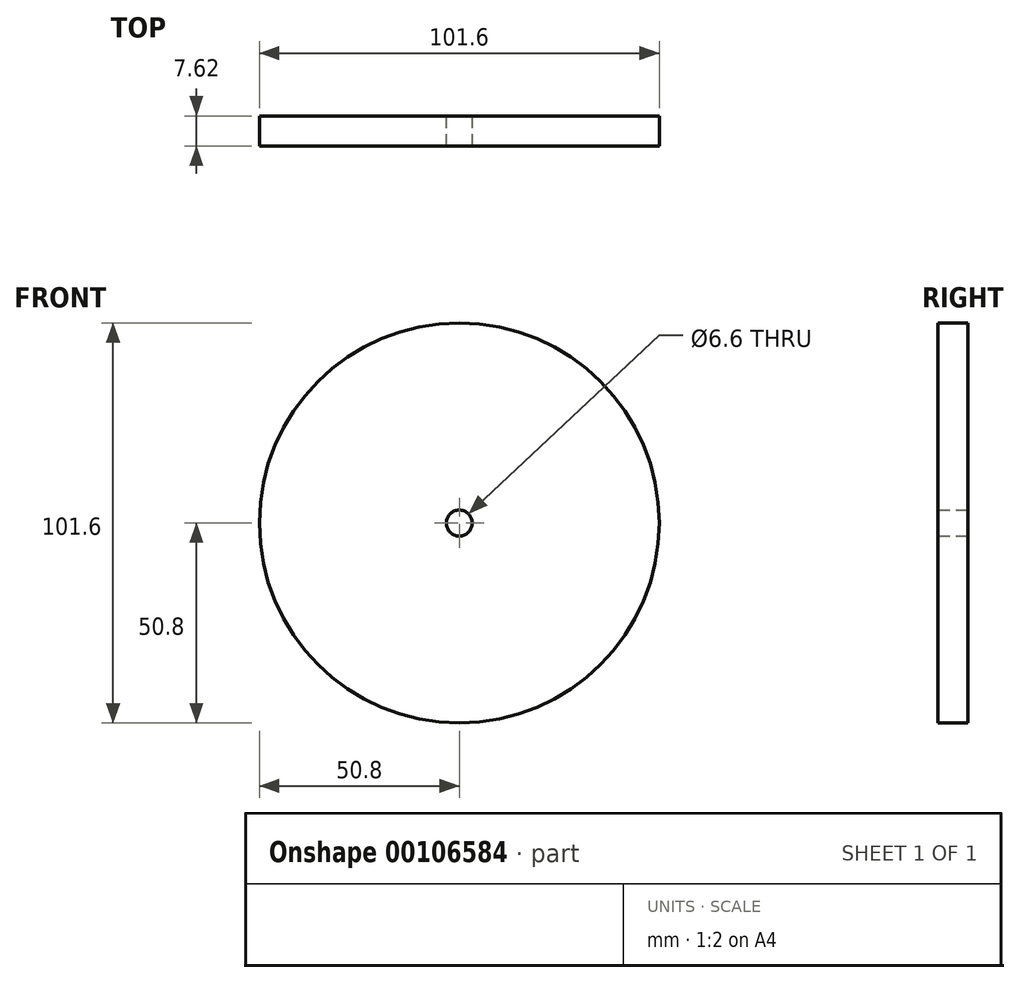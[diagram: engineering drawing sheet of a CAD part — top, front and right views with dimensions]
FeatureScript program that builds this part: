
annotation { "Feature Type Name" : "Feature", "Feature Type Description" : "" }
export const myFeature = defineFeature(function(context is Context, id is Id, definition is map)
    precondition{}
    {
        {
            var Q0;
            Q0=qCreatedBy(makeId("Front.planeOp"),FACE);
            var sketch = newSketch(context, id + "F0", { "sketchPlane" : qUnion([Q0])});
            skCircle(sketch, "E0", {"center": v(-24.16, 0) * mm, "radius": 50.8 * mm});
            skCircle(sketch, "E1", {"center": v(-24.16, 0) * mm, "radius": 3.3 * mm});
            skSolve(sketch);
        }
        {
            var Q0;
            Q0=makeQuery(id+"F0.imprint","IMPRINT",FACE,{"disambiguationData":[TD([[makeQuery(id+"F0.imprint","IMPRINT",EDGE,{"derivedFrom":sQuery(id+"F0.wireOp",EDGE,"E0")}),1.0]])]});
            extrude(context, id + "F1", {"entities" : qUnion([Q0]), "depth" : 7.62 * mm});
        }
    });
